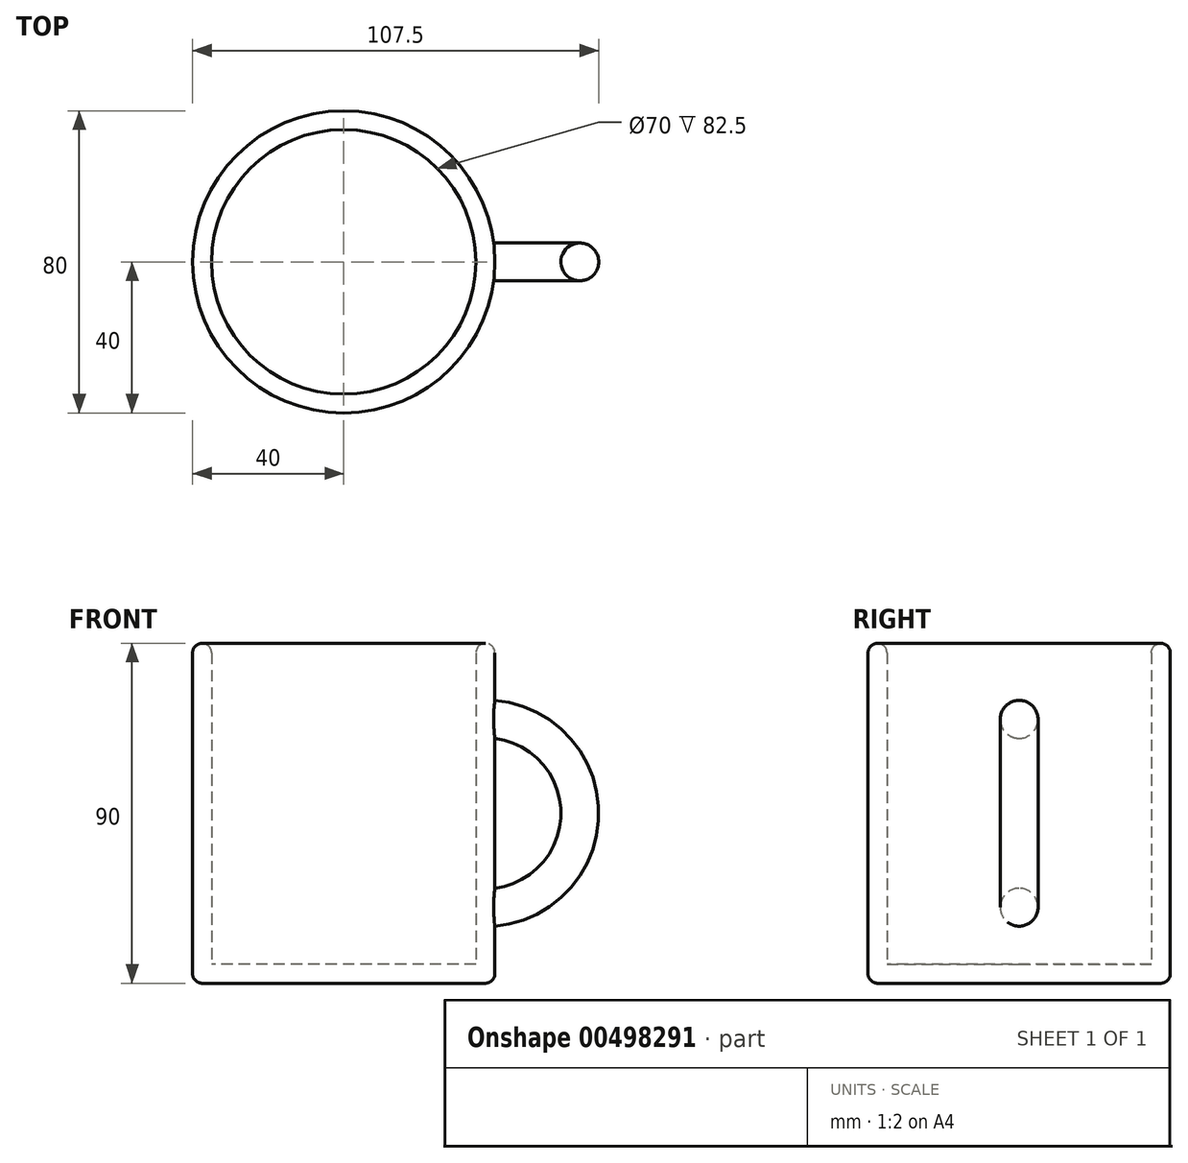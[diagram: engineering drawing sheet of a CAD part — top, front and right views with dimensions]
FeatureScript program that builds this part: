
annotation { "Feature Type Name" : "Feature", "Feature Type Description" : "" }
export const myFeature = defineFeature(function(context is Context, id is Id, definition is map)
    precondition{}
    {
        {
            var Q0;
            Q0=qCreatedBy(makeId("Top.planeOp"),FACE);
            var sketch = newSketch(context, id + "F0", { "sketchPlane" : qUnion([Q0])});
            skCircle(sketch, "E0", {"center": v(0, 0) * mm, "radius": 40 * mm});
            skSolve(sketch);
        }
        {
            var Q0;
            Q0=makeQuery(id+"F0.imprint","IMPRINT",FACE,{"disambiguationData":[TD([[makeQuery(id+"F0.imprint","IMPRINT",EDGE,{"derivedFrom":sQuery(id+"F0.wireOp",EDGE,"E0")}),1.0]])]});
            extrude(context, id + "F1", {"entities" : qUnion([Q0]), "depth" : 90 * mm});
        }
        {
            var Q0;
            Q0=makeQuery(id+"F1.opExtrude","CAP_FACE",FACE,{"disambiguationData":[OSD([sQuery(id+"F0.wireOp",EDGE,"E0")])],"isStart":false});
            shell(context, id + "F2", {"entities" : qUnion([Q0]), "thickness" : 5 * mm});
        }
        {
            var Q0;
            Q0=qCreatedBy(makeId("Right.planeOp"),FACE);
            cPlane(context, id + "F3", {"entities" : qUnion([Q0]), "cplaneType" : CPlaneType.OFFSET, "offset" : 37.5 * mm, "width" : 150 * mm, "height" : 150 * mm});
        }
        {
            var Q0;
            Q0=qCreatedBy(id+"F3.planeOp",FACE);
            var sketch = newSketch(context, id + "F4", { "sketchPlane" : qUnion([Q0])});
            skCircle(sketch, "E1", {"center": v(0, 70) * mm, "radius": 5 * mm});
            skLineSegment(sketch, "E2", {"start": v(0, 45) * mm, "end": v(66.59, 45) * mm});
            skSolve(sketch);
        }
        {
            var Q0;
            Q0 = qSketchRegion(id + "F4", true);
            var Q1;
            Q1=sQuery(id+"F4.wireOp",EDGE,"E2");
            revolve(context, id + "F5", {"operationType" : NewBodyOperationType.ADD, "entities" : qUnion([Q0]), "axis" : qUnion([Q1]), "revolveType" : RevolveType.ONE_DIRECTION, "angle" : 180 * degree});
        }
        {
            var Q0;
            Q0=makeQuery(id+"F1.opExtrude","CAP_EDGE",EDGE,{"disambiguationData":[OSD([sQuery(id+"F0.wireOp",EDGE,"E0")])],"isStart":false});
            var Q1;
            {var subQ0=sQuery(id+"F0.wireOp",EDGE,"E0");Q1=makeQuery(id+"F2.opShell","OFFSET_EDGE",EDGE,{"disambiguationData":[OSD([subQ0]),TDD([makeQuery(id+"F1.opExtrude","CAP_EDGE",EDGE,{"disambiguationData":[OSD([subQ0])],"isStart":false})])]});}
            fillet(context, id + "F6", {"entities" : qUnion([Q0, Q1]), "radius" : 2.5 * mm, "tangentPropagation" : true, "allowEdgeOverflow" : false});
        }
        {
            var Q0;
            Q0=makeQuery(id+"F1.opExtrude","CAP_EDGE",EDGE,{"disambiguationData":[OSD([sQuery(id+"F0.wireOp",EDGE,"E0")])],"isStart":true});
            fillet(context, id + "F7", {"entities" : qUnion([Q0]), "radius" : 2.5 * mm, "tangentPropagation" : true, "allowEdgeOverflow" : false});
        }
    });
